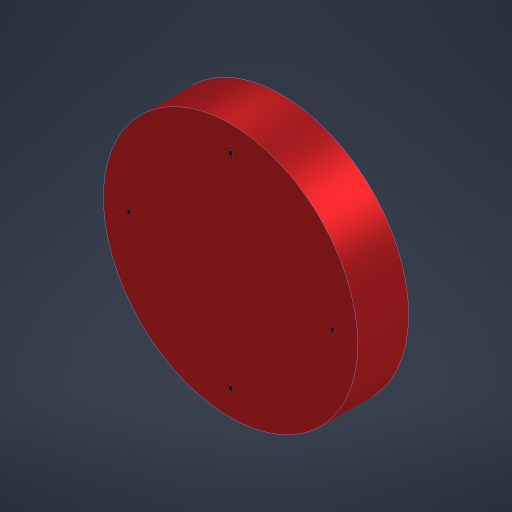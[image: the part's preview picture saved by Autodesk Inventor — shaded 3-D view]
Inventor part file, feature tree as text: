
AUTODESK INVENTOR PART (.ipt)
format: ipt  version: 2023 (Build 270158000, 158)  size: 239,616 bytes
history: native  units: mm
features: extrude x5, sketch x4, fillet x1, direct_edit x1, other x1
ambient origin geometry x8: Origin, YZ Plane, XZ Plane, XY Plane, X Axis, Y Axis, Z Axis, Center Point
bodies: Solid1 (feature_tree)
feature tree (12):
  extrude  "Extrusion1"  Depth=200.0mm
  fillet  "Fillet1"  Radius=30.0mm
  extrude  "Extrusion2"  Depth=30.0mm
  sketch  "Sketch11"  dims[d5=30.0mm d6=30.0mm]
  extrude  "Extrusion10"  Depth=30.0mm
  extrude  "Extrusion11"  Depth=10.0mm
  direct_edit  "Direct Edit3"
  extrude  "Extrusion12"  Depth=10.0mm
  sketch  "Sketch1"  dims[d0=200.0mm d1=200.0mm d2=30.0mm]
  sketch  "Sketch2"  dims[d3=30.0mm d4=30.0mm]
  sketch  "Sketch13"  dims[d7=30.0mm d8=30.0mm d9=30.0mm d10=10.0mm d11=0.0mm d12=10.0mm d13=125.0mm d14=15.0mm d15=0.0mm d145=200.0mm d146=0.0mm d147=200.0mm d148=0.0mm d149=15.0mm d150=10.0mm d151=10.0mm d153=3.0mm d154=3.0mm d155=3.0mm d156=3.0mm d157=200.0mm d158=0.0mm d64=0.5mm d65=0.872665mm d66=0.5mm d67=0.872665mm]
  other  "Scale3"
